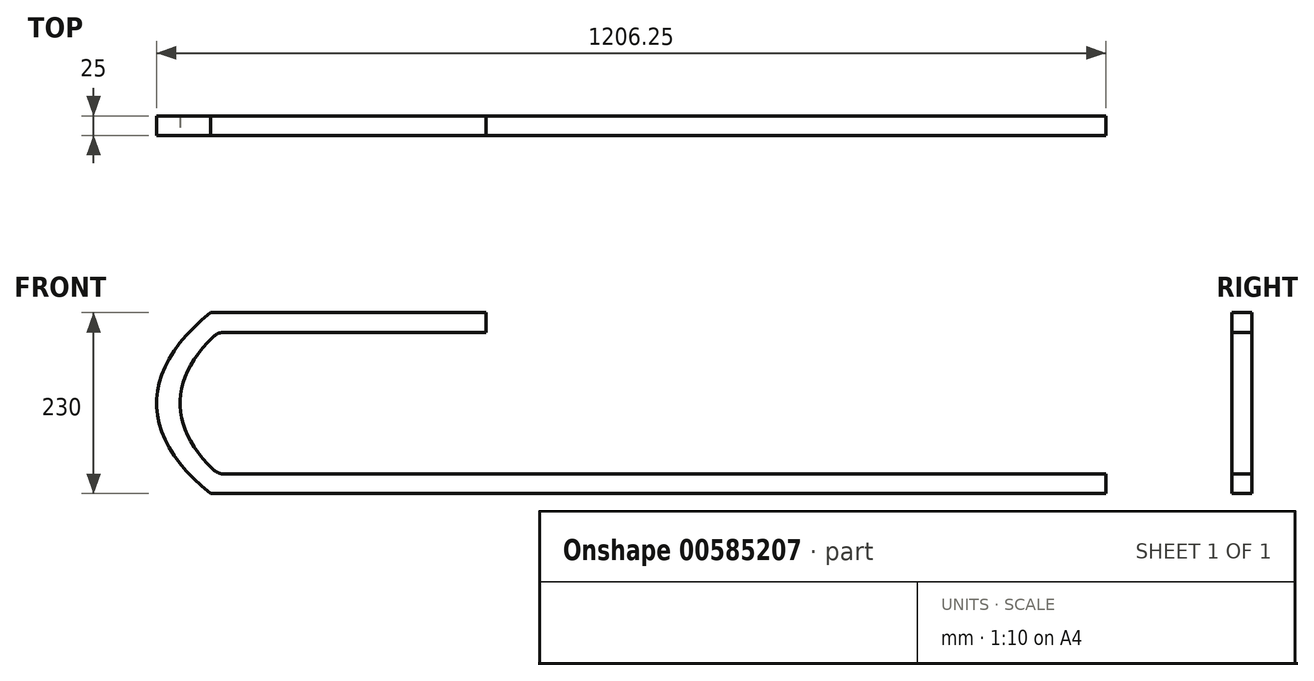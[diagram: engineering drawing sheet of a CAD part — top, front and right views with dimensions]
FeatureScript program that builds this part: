
annotation { "Feature Type Name" : "Feature", "Feature Type Description" : "" }
export const myFeature = defineFeature(function(context is Context, id is Id, definition is map)
    precondition{}
    {
        {
            var Q0;
            Q0=qCreatedBy(makeId("Front.planeOp"),FACE);
            var sketch = newSketch(context, id + "F0", { "sketchPlane" : qUnion([Q0])});
            skLineSegment(sketch, "E0", {"start": v(0, 0) * mm, "end": v(1137.5, 0) * mm});
            skLineSegment(sketch, "E1", {"start": v(1137.5, 25) * mm, "end": v(1137.5, 0) * mm});
            skLineSegment(sketch, "E2", {"start": v(1137.5, 25) * mm, "end": v(9.16, 25) * mm});
            skEllipse(sketch, "E3", {"center": v(831.25, 115) * mm, "majorRadius": 900 * mm, "minorRadius": 300 * mm, "majorAxis": v(-1, 0)});
            skEllipse(sketch, "E4", {"center": v(831.25, 115) * mm, "majorRadius": 870 * mm, "minorRadius": 275 * mm, "majorAxis": v(-1, 0)});
            skLineSegment(sketch, "E5", {"start": v(831.25, 115) * mm, "end": v(-68.75, 115) * mm, "construction": true});
            skLineSegment(sketch, "E6", {"start": v(-38.75, 115) * mm, "end": v(-68.75, 115) * mm, "construction": true});
            skLineSegment(sketch, "E7", {"start": v(831.25, 115) * mm, "end": v(831.25, -185) * mm, "construction": true});
            skLineSegment(sketch, "E8", {"start": v(831.25, -160) * mm, "end": v(831.25, -185) * mm, "construction": true});
            skLineSegment(sketch, "E9", {"start": v(0, 0) * mm, "end": v(0, 115) * mm, "construction": true});
            skLineSegment(sketch, "E10", {"start": v(0, 115) * mm, "end": v(0, 230) * mm, "construction": true});
            skLineSegment(sketch, "E11", {"start": v(0, 230) * mm, "end": v(350, 230) * mm});
            skLineSegment(sketch, "E12", {"start": v(350, 205) * mm, "end": v(350, 230) * mm});
            skLineSegment(sketch, "E13", {"start": v(350, 205) * mm, "end": v(9.16, 205) * mm});
            skSolve(sketch);
        }
        {
            var Q0;
            {var subQ4=sQuery(id+"F0.wireOp",EDGE,"E12");Q0=makeQuery(id+"F0.imprint","IMPRINT",FACE,{"disambiguationData":[TD([[makeQuery(id+"F0.imprint","IMPRINT",EDGE,{"derivedFrom":subQ4}),1.0]])]});}
            var Q1;
            {var subQ5=sQuery(id+"F0.wireOp",EDGE,"E0");var subQ7=sQuery(id+"F0.wireOp",EDGE,"E3");var subQ8=makeQuery(id+"F0.imprint","INTERSECT",VERTEX,{"derivedFrom":[subQ5,subQ7]});Q1=makeQuery(id+"F0.imprint","IMPRINT",FACE,{"disambiguationData":[TD([[makeQuery(id+"F0.imprint","IMPRINT",EDGE,{"disambiguationData":[TD([[subQ8,-1.0]])],"derivedFrom":subQ5}),1.0]])]});}
            var Q2;
            {var subQ0=sQuery(id+"F0.wireOp",EDGE,"E1");Q2=makeQuery(id+"F0.imprint","IMPRINT",FACE,{"disambiguationData":[TD([[makeQuery(id+"F0.imprint","IMPRINT",EDGE,{"derivedFrom":subQ0}),-1.0]])]});}
            extrude(context, id + "F1", {"entities" : qUnion([Q0, Q1, Q2]), "endBound" : BoundingType.SYMMETRIC, "depth" : 25 * mm, "offsetDistance" : 25 * mm});
        }
        {
            var Q0;
            Q0=makeQuery(id+"F1.opExtrude","SWEPT_EDGE",EDGE,{"disambiguationData":[OSD([sQuery(id+"F0.wireOp",EDGE,"E2"),sQuery(id+"F0.wireOp",EDGE,"E4")])]});
            var Q1;
            Q1=makeQuery(id+"F1.opExtrude","SWEPT_EDGE",EDGE,{"disambiguationData":[OSD([sQuery(id+"F0.wireOp",EDGE,"E4"),sQuery(id+"F0.wireOp",EDGE,"E13")])]});
            fillet(context, id + "F2", {"entities" : qUnion([Q0, Q1]), "radius" : 20 * mm, "tangentPropagation" : true, "allowEdgeOverflow" : false});
        }
    });
